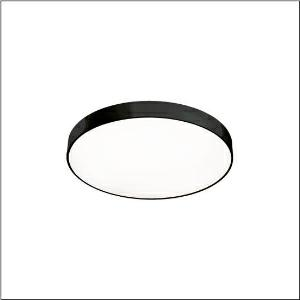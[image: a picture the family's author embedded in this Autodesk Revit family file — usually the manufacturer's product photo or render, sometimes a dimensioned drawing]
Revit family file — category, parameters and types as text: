
# Revit family: round_21_m_51mr36fd0321b
name_source: partatom
category: Lighting Fixtures
units: mm (PartAtom-declared; Revit-internal decimal feet)

## family parameters
Cut with Voids When Loaded = No
Host = Face
Light Source = No
Part Type = Normal
Room Calculation Point = No
Round Connector Dimension = Use Diameter
Shared = No

## types (1)
- Round 21 M (1 x LED, 6790 lm, 54.8 W, 3000K)
    Apparent Load = 55 VA
    CIE Flux Codes = 49 80 96 100 100
    Color Rendering = 80
    Color Temperature = 3000K
    Default Elevation = 1800 mm
    Description = Round 21 M, wall and ceiling luminaire, primary optical cover: cover, of PMMA, opal, light emission: direct distribution, primary light characteristic: symmetric, installation type: suspended mounting, surface-mounted, LED, rated luminous flux: 6.790lm, luminous efficacy: 124lm/W, light colour: 830, colour temperature: 3000K, with terminal, 5-pole, mains connection: 230V, AC, 50/60Hz, rated input power: 55W, housing, of aluminium, coated, black, diameter: 600mm, height: 62mm, protection rating (complete): IP40, insulation class (complete): insulation class I (protective earthing), certification: CE, impact resistance: IK04, permissible operating ambient temperature: -10..+35°C, packaging unit: 1 piece
    Height = 87 mm
    Lamp = 1 x LED
    Lamp Light Flux = 6790 lm
    Lamp Power = 54.8 W
    Lamp count = 1
    Length = 600 mm
    Luminous efficacy = 124 lm/W
    Manufacturer = Siteco
    ModVariant = No
    Model = 51MR36FD0321B
    Mounting Place = Ceiling
    Mounting Type = Surface mounted
    Number of Poles = 1
    OnlyDefault = Yes
    Power Factor = 1
    Product Name = Round 21 M
    Product group = wall and ceiling luminaire
    ProductGroupID = 301
    Protection Class = Protection class I
    Protection Degree = IP 40
    RLX_Detail_Level = 1
    RLX_Emergency_Light_Flux = 0 lm
    RLX_Emergency_Type = 0
    RLX_Emergency_Type_DB = No
    RlxData = <blob elided: 17705 chars, md5=935f0cfd>
    Socket = socket
    Standby Power = 0 W
    System Light Flux = 6790 lm
    System Power = 55 W
    Type Comments = Product without accessories
    Type Image = l_1258332.jpg
    URL = http://relux.com
    VarID = ---
    Voltage = 0 V
    Weight = 0.00 kg
    Width = 0 mm  [stored 0 ft]

note: [stored X ft] marks values corroborated as IEEE doubles in the binary element streams (Revit-internal decimal feet)

## geometry (parser evidence)
native form markers: Blend x4, Sweep x12
no freeform markers — native parametric forms only
